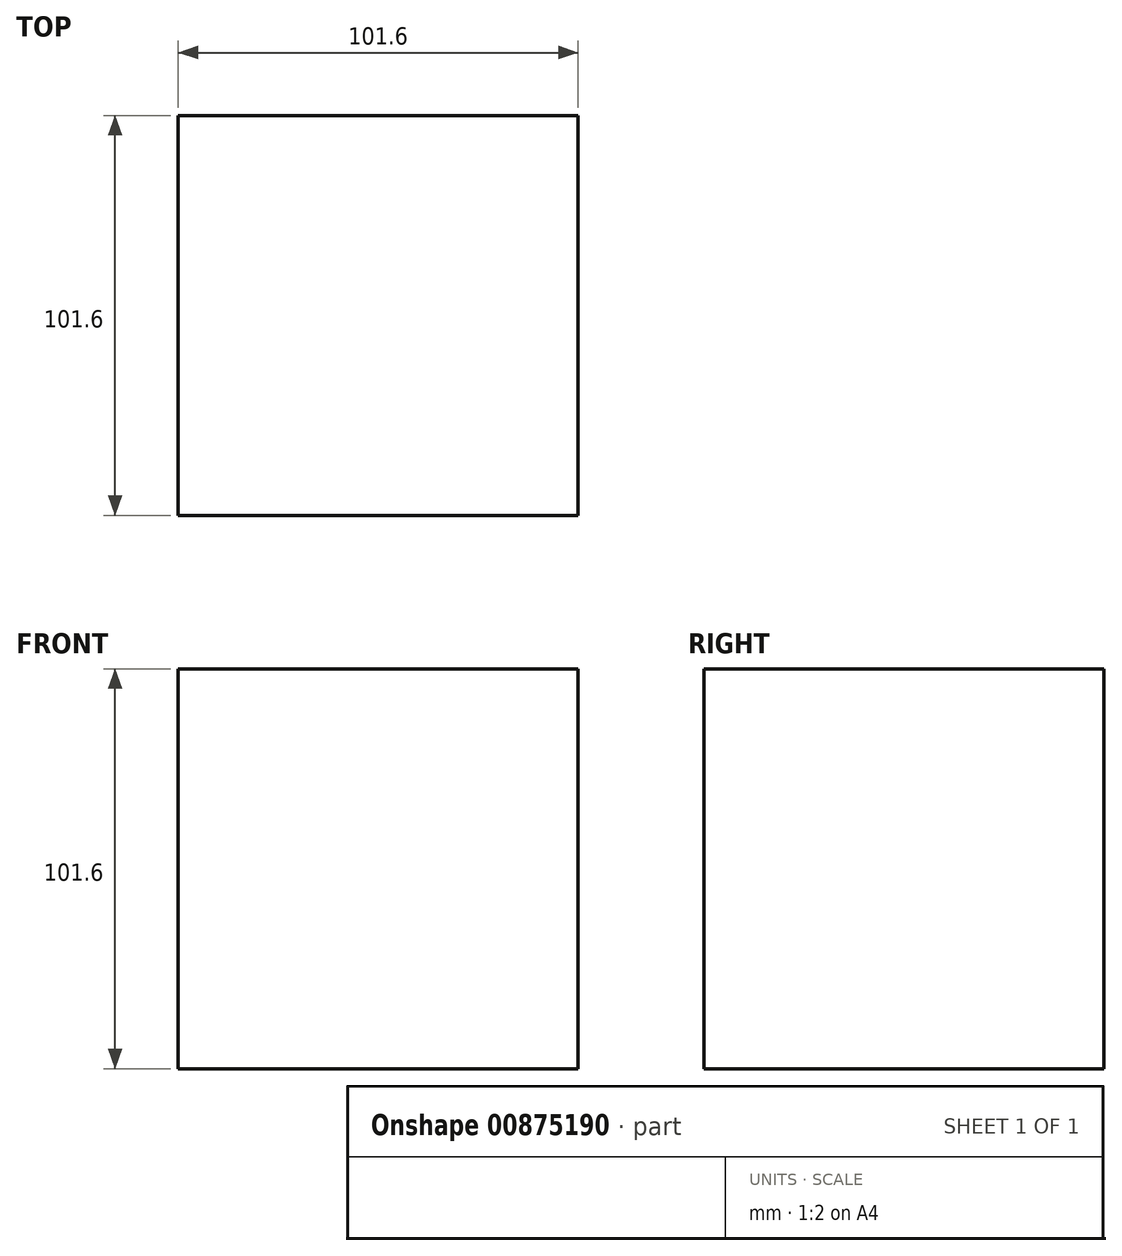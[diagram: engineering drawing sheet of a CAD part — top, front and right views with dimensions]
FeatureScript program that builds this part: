
annotation { "Feature Type Name" : "Feature", "Feature Type Description" : "" }
export const myFeature = defineFeature(function(context is Context, id is Id, definition is map)
    precondition{}
    {
        {
            var Q0;
            Q0=qCreatedBy(makeId("Top.planeOp"),FACE);
            var sketch = newSketch(context, id + "F0", { "sketchPlane" : qUnion([Q0])});
            skLineSegment(sketch, "E0.bottom", {"start": v(-53.07, 48.91) * mm, "end": v(48.53, 48.91) * mm});
            skLineSegment(sketch, "E0.top", {"start": v(-53.07, -52.69) * mm, "end": v(48.53, -52.69) * mm});
            skLineSegment(sketch, "E0.left", {"start": v(-53.07, 48.91) * mm, "end": v(-53.07, -52.69) * mm});
            skLineSegment(sketch, "E0.right", {"start": v(48.53, 48.91) * mm, "end": v(48.53, -52.69) * mm});
            skSolve(sketch);
        }
        {
            var Q0;
            Q0 = qSketchRegion(id + "F0", true);
            extrude(context, id + "F1", {"entities" : qUnion([Q0]), "depth" : 101.6 * mm, "offsetDistance" : 25.4 * mm});
        }
    });
